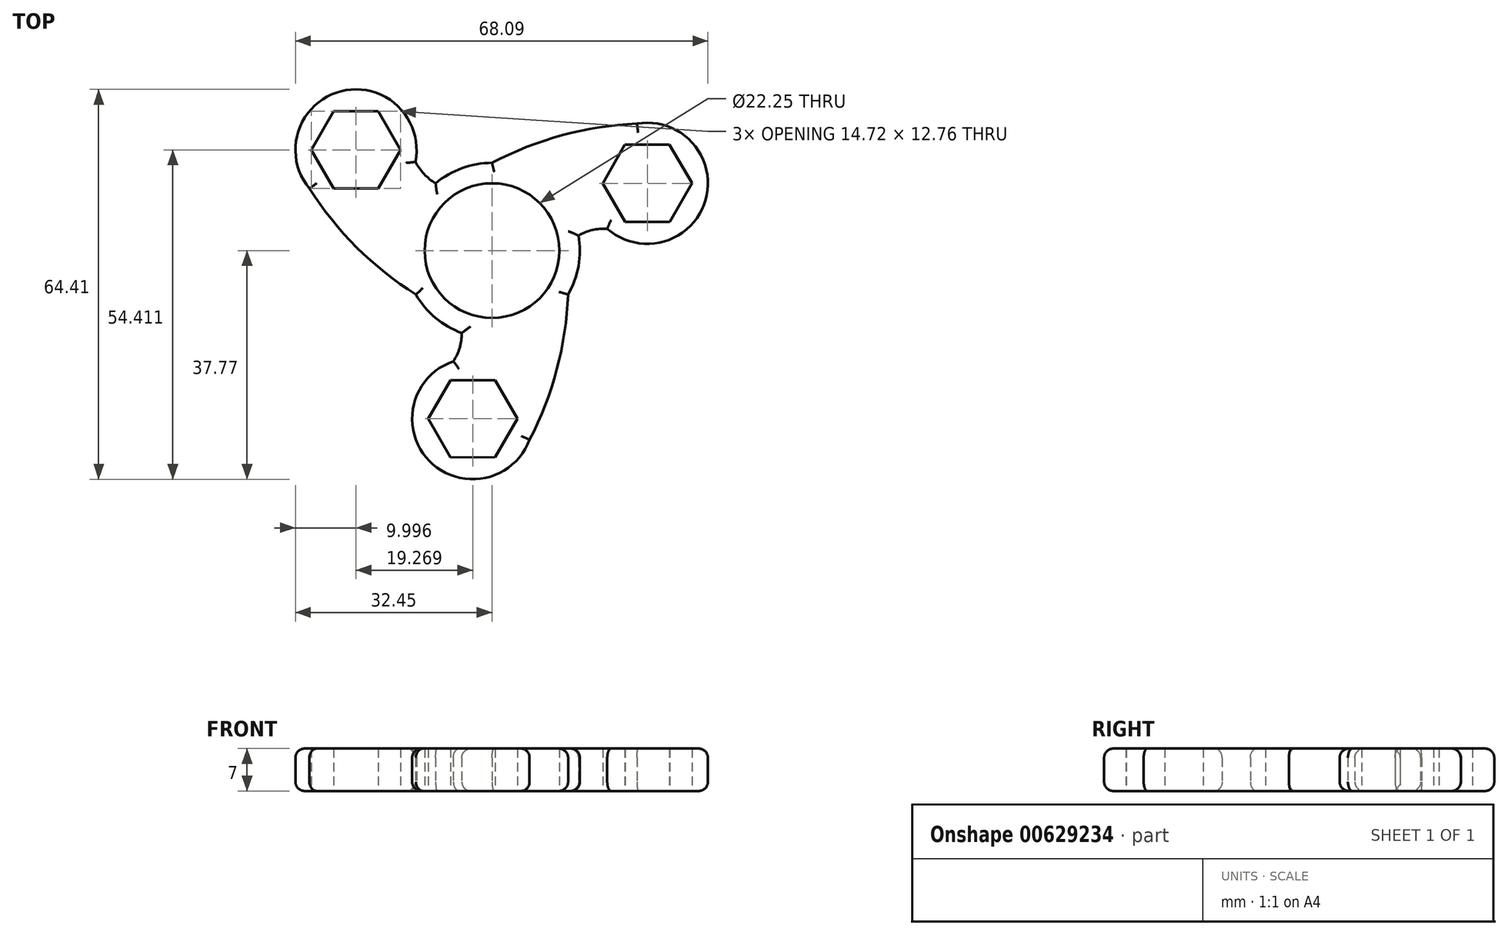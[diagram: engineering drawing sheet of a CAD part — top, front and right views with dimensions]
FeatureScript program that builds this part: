
annotation { "Feature Type Name" : "Feature", "Feature Type Description" : "" }
export const myFeature = defineFeature(function(context is Context, id is Id, definition is map)
    precondition{}
    {
        {
            var Q0;
            Q0=qCreatedBy(makeId("Top.planeOp"),FACE);
            var sketch = newSketch(context, id + "F0", { "sketchPlane" : qUnion([Q0])});
            skCircle(sketch, "E0", {"center": v(0, 0) * mm, "radius": 11.12 * mm});
            skCircle(sketch, "E1", {"center": v(0, 0) * mm, "radius": 14.5 * mm});
            skCircle(sketch, "E2.cCircle", {"center": v(25.64, 11.12) * mm, "radius": 6.38 * mm, "construction": true});
            skLineSegment(sketch, "E2.0", {"start": v(18.28, 11.12) * mm, "end": v(21.95, 17.5) * mm});
            skLineSegment(sketch, "E2.1", {"start": v(21.95, 17.5) * mm, "end": v(29.31, 17.5) * mm});
            skLineSegment(sketch, "E2.2", {"start": v(29.31, 17.5) * mm, "end": v(33, 11.13) * mm});
            skLineSegment(sketch, "E2.3", {"start": v(33, 11.13) * mm, "end": v(29.33, 4.75) * mm});
            skLineSegment(sketch, "E2.4", {"start": v(29.33, 4.75) * mm, "end": v(21.97, 4.75) * mm});
            skLineSegment(sketch, "E2.5", {"start": v(21.97, 4.75) * mm, "end": v(18.28, 11.12) * mm});
            skPoint(sketch, "E2.0.midPoint", {"position": v(20.11, 14.3) * mm});
            skCircle(sketch, "E3", {"center": v(25.64, 11.12) * mm, "radius": 10 * mm});
            skArc(sketch, "E4", {"start": v(19.03, 3.62) * mm, "mid": v(16.57, 3.4) * mm, "end": v(14.28, 2.49) * mm});
            skArc(sketch, "E5", {"start": v(27.01, 21.03) * mm, "mid": v(13.1, 19.45) * mm, "end": v(0, 14.5) * mm});
            skLineSegment(sketch, "E6.1.0", {"start": v(-29.81, 16.63) * mm, "end": v(-26.14, 23.01) * mm});
            skLineSegment(sketch, "E6.1.1", {"start": v(-15.1, 16.65) * mm, "end": v(-18.76, 10.27) * mm});
            skLineSegment(sketch, "E6.1.2", {"start": v(-26.14, 23.01) * mm, "end": v(-18.78, 23.02) * mm});
            skPoint(sketch, "E6.1.3", {"position": v(-22.45, 10.27) * mm});
            skLineSegment(sketch, "E6.1.4", {"start": v(-26.13, 10.26) * mm, "end": v(-29.81, 16.63) * mm});
            skArc(sketch, "E6.1.5", {"start": v(-12.65, 14.66) * mm, "mid": v(-11.23, 12.66) * mm, "end": v(-9.3, 11.13) * mm});
            skCircle(sketch, "E6.1.6", {"center": v(-22.45, 16.64) * mm, "radius": 10 * mm});
            skCircle(sketch, "E6.1.7", {"center": v(-22.45, 16.64) * mm, "radius": 6.38 * mm, "construction": true});
            skLineSegment(sketch, "E6.1.8", {"start": v(-18.76, 10.27) * mm, "end": v(-26.13, 10.26) * mm});
            skLineSegment(sketch, "E6.1.9", {"start": v(-18.78, 23.02) * mm, "end": v(-15.1, 16.65) * mm});
            skArc(sketch, "E6.1.10", {"start": v(-31.72, 12.88) * mm, "mid": v(-23.4, 1.62) * mm, "end": v(-12.56, -7.25) * mm});
            skLineSegment(sketch, "E6.2.0", {"start": v(0.5, -34.14) * mm, "end": v(-6.86, -34.15) * mm});
            skLineSegment(sketch, "E6.2.1", {"start": v(-6.87, -21.4) * mm, "end": v(0.49, -21.39) * mm});
            skLineSegment(sketch, "E6.2.2", {"start": v(-6.86, -34.15) * mm, "end": v(-10.55, -27.78) * mm});
            skPoint(sketch, "E6.2.3", {"position": v(2.33, -24.57) * mm});
            skLineSegment(sketch, "E6.2.4", {"start": v(4.18, -27.76) * mm, "end": v(0.5, -34.14) * mm});
            skArc(sketch, "E6.2.5", {"start": v(-6.37, -18.29) * mm, "mid": v(-5.35, -16.05) * mm, "end": v(-4.99, -13.62) * mm});
            skCircle(sketch, "E6.2.6", {"center": v(-3.18, -27.77) * mm, "radius": 10 * mm});
            skCircle(sketch, "E6.2.7", {"center": v(-3.18, -27.77) * mm, "radius": 6.38 * mm, "construction": true});
            skLineSegment(sketch, "E6.2.8", {"start": v(0.49, -21.39) * mm, "end": v(4.18, -27.76) * mm});
            skLineSegment(sketch, "E6.2.9", {"start": v(-10.55, -27.78) * mm, "end": v(-6.87, -21.4) * mm});
            skArc(sketch, "E6.2.10", {"start": v(4.7, -33.9) * mm, "mid": v(10.3, -21.07) * mm, "end": v(12.56, -7.25) * mm});
            skSolve(sketch);
        }
        {
            var Q0;
            Q0=makeQuery(id+"F0.imprint","IMPRINT",FACE,{"disambiguationData":[TD([[makeQuery(id+"F0.imprint","IMPRINT",EDGE,{"derivedFrom":sQuery(id+"F0.wireOp",EDGE,"E0")}),-1.0]])]});
            var Q1;
            Q1=makeQuery(id+"F0.imprint","IMPRINT",FACE,{"disambiguationData":[TD([[makeQuery(id+"F0.imprint","IMPRINT",EDGE,{"derivedFrom":sQuery(id+"F0.wireOp",EDGE,"E6.2.0")}),1.0]])]});
            var Q2;
            Q2=makeQuery(id+"F0.imprint","IMPRINT",FACE,{"disambiguationData":[TD([[makeQuery(id+"F0.imprint","IMPRINT",EDGE,{"derivedFrom":sQuery(id+"F0.wireOp",EDGE,"E6.1.0")}),1.0]])]});
            var Q3;
            Q3=makeQuery(id+"F0.imprint","IMPRINT",FACE,{"disambiguationData":[TD([[makeQuery(id+"F0.imprint","IMPRINT",EDGE,{"derivedFrom":sQuery(id+"F0.wireOp",EDGE,"E2.0")}),1.0]])]});
            var Q4;
            {var subQ0=sQuery(id+"F0.wireOp",EDGE,"E6.2.5");Q4=makeQuery(id+"F0.imprint","IMPRINT",FACE,{"disambiguationData":[TD([[makeQuery(id+"F0.imprint","IMPRINT",EDGE,{"derivedFrom":subQ0}),-1.0]])]});}
            var Q5;
            {var subQ0=sQuery(id+"F0.wireOp",EDGE,"E6.1.5");Q5=makeQuery(id+"F0.imprint","IMPRINT",FACE,{"disambiguationData":[TD([[makeQuery(id+"F0.imprint","IMPRINT",EDGE,{"derivedFrom":subQ0}),-1.0]])]});}
            var Q6;
            {var subQ0=sQuery(id+"F0.wireOp",EDGE,"E4");Q6=makeQuery(id+"F0.imprint","IMPRINT",FACE,{"disambiguationData":[TD([[makeQuery(id+"F0.imprint","IMPRINT",EDGE,{"derivedFrom":subQ0}),-1.0]])]});}
            var Q7;
            {var subQ0=sQuery(id+"F0.wireOp",EDGE,"E6.2.10");var subQ1=sQuery(id+"F0.wireOp",EDGE,"E6.2.6");var subQ2=makeQuery(id+"F0.imprint","INTERSECT",VERTEX,{"disambiguationData":[OD(0.0)],"derivedFrom":[subQ1,subQ0]});Q7=makeQuery(id+"F0.imprint","IMPRINT",FACE,{"disambiguationData":[TD([[makeQuery(id+"F0.imprint","IMPRINT",EDGE,{"disambiguationData":[TD([[subQ2,-1.0]])],"derivedFrom":subQ1}),1.0]])]});}
            var Q8;
            {var subQ0=sQuery(id+"F0.wireOp",EDGE,"E6.1.10");var subQ1=sQuery(id+"F0.wireOp",EDGE,"E6.1.6");var subQ2=makeQuery(id+"F0.imprint","INTERSECT",VERTEX,{"disambiguationData":[OD(0.0)],"derivedFrom":[subQ1,subQ0]});Q8=makeQuery(id+"F0.imprint","IMPRINT",FACE,{"disambiguationData":[TD([[makeQuery(id+"F0.imprint","IMPRINT",EDGE,{"disambiguationData":[TD([[subQ2,-1.0]])],"derivedFrom":subQ1}),1.0]])]});}
            var Q9;
            {var subQ0=sQuery(id+"F0.wireOp",EDGE,"E5");var subQ1=sQuery(id+"F0.wireOp",EDGE,"E3");var subQ2=makeQuery(id+"F0.imprint","INTERSECT",VERTEX,{"disambiguationData":[OD(0.0)],"derivedFrom":[subQ1,subQ0]});Q9=makeQuery(id+"F0.imprint","IMPRINT",FACE,{"disambiguationData":[TD([[makeQuery(id+"F0.imprint","IMPRINT",EDGE,{"disambiguationData":[TD([[subQ2,-1.0]])],"derivedFrom":subQ1}),1.0]])]});}
            extrude(context, id + "F1", {"entities" : qUnion([Q0, Q1, Q2, Q3, Q4, Q5, Q6, Q7, Q8, Q9]), "depth" : 7 * mm, "offsetDistance" : 25 * mm});
        }
        {
            var Q0;
            Q0=makeQuery(id+"F1.opExtrude","CAP_EDGE",EDGE,{"disambiguationData":[OSD([sQuery(id+"F0.wireOp",EDGE,"E5")])],"isStart":false});
            var Q1;
            Q1=makeQuery(id+"F1.opExtrude","CAP_EDGE",EDGE,{"disambiguationData":[OSD([sQuery(id+"F0.wireOp",EDGE,"E4")])],"isStart":false});
            var Q2;
            Q2=makeQuery(id+"F1.opExtrude","CAP_EDGE",EDGE,{"disambiguationData":[OSD([sQuery(id+"F0.wireOp",EDGE,"E3")])],"isStart":false});
            var Q3;
            {var subQ0=sQuery(id+"F0.wireOp",EDGE,"E1");Q3=makeQuery(id+"F1.opExtrude","CAP_EDGE",EDGE,{"disambiguationData":[OSD([subQ0]),TDD([makeQuery(id+"F0.imprint","IMPRINT",EDGE,{"disambiguationData":[TD([[makeQuery(id+"F0.imprint","INTERSECT",VERTEX,{"derivedFrom":[subQ0,sQuery(id+"F0.wireOp",EDGE,"E4")]}),1.0]])],"derivedFrom":subQ0})])],"isStart":false});}
            var Q4;
            Q4=makeQuery(id+"F1.opExtrude","CAP_EDGE",EDGE,{"disambiguationData":[OSD([sQuery(id+"F0.wireOp",EDGE,"E6.2.10")])],"isStart":false});
            var Q5;
            Q5=makeQuery(id+"F1.opExtrude","CAP_EDGE",EDGE,{"disambiguationData":[OSD([sQuery(id+"F0.wireOp",EDGE,"E6.2.5")])],"isStart":false});
            var Q6;
            {var subQ0=sQuery(id+"F0.wireOp",EDGE,"E1");Q6=makeQuery(id+"F1.opExtrude","CAP_EDGE",EDGE,{"disambiguationData":[OSD([subQ0]),TDD([makeQuery(id+"F0.imprint","IMPRINT",EDGE,{"disambiguationData":[TD([[makeQuery(id+"F0.imprint","INTERSECT",VERTEX,{"derivedFrom":[subQ0,sQuery(id+"F0.wireOp",EDGE,"E6.1.10")]}),-1.0]])],"derivedFrom":subQ0})])],"isStart":false});}
            var Q7;
            Q7=makeQuery(id+"F1.opExtrude","CAP_EDGE",EDGE,{"disambiguationData":[OSD([sQuery(id+"F0.wireOp",EDGE,"E6.1.10")])],"isStart":false});
            var Q8;
            Q8=makeQuery(id+"F1.opExtrude","CAP_EDGE",EDGE,{"disambiguationData":[OSD([sQuery(id+"F0.wireOp",EDGE,"E6.1.6")])],"isStart":false});
            var Q9;
            Q9=makeQuery(id+"F1.opExtrude","CAP_EDGE",EDGE,{"disambiguationData":[OSD([sQuery(id+"F0.wireOp",EDGE,"E6.2.6")])],"isStart":false});
            var Q10;
            Q10=makeQuery(id+"F1.opExtrude","CAP_EDGE",EDGE,{"disambiguationData":[OSD([sQuery(id+"F0.wireOp",EDGE,"E6.1.5")])],"isStart":false});
            var Q11;
            {var subQ0=sQuery(id+"F0.wireOp",EDGE,"E1");Q11=makeQuery(id+"F1.opExtrude","CAP_EDGE",EDGE,{"disambiguationData":[OSD([subQ0]),TDD([makeQuery(id+"F0.imprint","IMPRINT",EDGE,{"disambiguationData":[TD([[makeQuery(id+"F0.imprint","INTERSECT",VERTEX,{"derivedFrom":[subQ0,sQuery(id+"F0.wireOp",EDGE,"E5")]}),-1.0]])],"derivedFrom":subQ0})])],"isStart":false});}
            fillet(context, id + "F2", {"entities" : qUnion([Q0, Q1, Q2, Q3, Q4, Q5, Q6, Q7, Q8, Q9, Q10, Q11]), "radius" : 1.5 * mm, "tangentPropagation" : true, "allowEdgeOverflow" : false});
        }
        {
            var Q0;
            Q0=makeQuery(id+"F1.opExtrude","CAP_EDGE",EDGE,{"disambiguationData":[OSD([sQuery(id+"F0.wireOp",EDGE,"E6.2.6")])],"isStart":true});
            var Q1;
            Q1=makeQuery(id+"F1.opExtrude","CAP_EDGE",EDGE,{"disambiguationData":[OSD([sQuery(id+"F0.wireOp",EDGE,"E6.2.5")])],"isStart":true});
            var Q2;
            {var subQ0=sQuery(id+"F0.wireOp",EDGE,"E1");Q2=makeQuery(id+"F1.opExtrude","CAP_EDGE",EDGE,{"disambiguationData":[OSD([subQ0]),TDD([makeQuery(id+"F0.imprint","IMPRINT",EDGE,{"disambiguationData":[TD([[makeQuery(id+"F0.imprint","INTERSECT",VERTEX,{"derivedFrom":[subQ0,sQuery(id+"F0.wireOp",EDGE,"E6.1.10")]}),-1.0]])],"derivedFrom":subQ0})])],"isStart":true});}
            var Q3;
            Q3=makeQuery(id+"F1.opExtrude","CAP_EDGE",EDGE,{"disambiguationData":[OSD([sQuery(id+"F0.wireOp",EDGE,"E6.1.10")])],"isStart":true});
            var Q4;
            Q4=makeQuery(id+"F1.opExtrude","CAP_EDGE",EDGE,{"disambiguationData":[OSD([sQuery(id+"F0.wireOp",EDGE,"E6.1.5")])],"isStart":true});
            var Q5;
            Q5=makeQuery(id+"F1.opExtrude","CAP_EDGE",EDGE,{"disambiguationData":[OSD([sQuery(id+"F0.wireOp",EDGE,"E6.1.6")])],"isStart":true});
            var Q6;
            {var subQ0=sQuery(id+"F0.wireOp",EDGE,"E1");Q6=makeQuery(id+"F1.opExtrude","CAP_EDGE",EDGE,{"disambiguationData":[OSD([subQ0]),TDD([makeQuery(id+"F0.imprint","IMPRINT",EDGE,{"disambiguationData":[TD([[makeQuery(id+"F0.imprint","INTERSECT",VERTEX,{"derivedFrom":[subQ0,sQuery(id+"F0.wireOp",EDGE,"E5")]}),-1.0]])],"derivedFrom":subQ0})])],"isStart":true});}
            var Q7;
            Q7=makeQuery(id+"F1.opExtrude","CAP_EDGE",EDGE,{"disambiguationData":[OSD([sQuery(id+"F0.wireOp",EDGE,"E5")])],"isStart":true});
            var Q8;
            Q8=makeQuery(id+"F1.opExtrude","CAP_EDGE",EDGE,{"disambiguationData":[OSD([sQuery(id+"F0.wireOp",EDGE,"E3")])],"isStart":true});
            var Q9;
            Q9=makeQuery(id+"F1.opExtrude","CAP_EDGE",EDGE,{"disambiguationData":[OSD([sQuery(id+"F0.wireOp",EDGE,"E4")])],"isStart":true});
            var Q10;
            {var subQ0=sQuery(id+"F0.wireOp",EDGE,"E1");Q10=makeQuery(id+"F1.opExtrude","CAP_EDGE",EDGE,{"disambiguationData":[OSD([subQ0]),TDD([makeQuery(id+"F0.imprint","IMPRINT",EDGE,{"disambiguationData":[TD([[makeQuery(id+"F0.imprint","INTERSECT",VERTEX,{"derivedFrom":[subQ0,sQuery(id+"F0.wireOp",EDGE,"E4")]}),1.0]])],"derivedFrom":subQ0})])],"isStart":true});}
            var Q11;
            Q11=makeQuery(id+"F1.opExtrude","CAP_EDGE",EDGE,{"disambiguationData":[OSD([sQuery(id+"F0.wireOp",EDGE,"E6.2.10")])],"isStart":true});
            fillet(context, id + "F3", {"entities" : qUnion([Q0, Q1, Q2, Q3, Q4, Q5, Q6, Q7, Q8, Q9, Q10, Q11]), "radius" : 1.5 * mm, "tangentPropagation" : true, "allowEdgeOverflow" : false});
        }
    });
